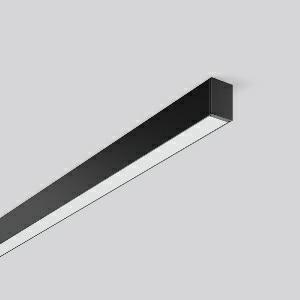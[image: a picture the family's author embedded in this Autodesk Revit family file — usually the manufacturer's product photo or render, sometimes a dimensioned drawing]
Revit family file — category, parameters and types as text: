
# Revit family: less_is_more_27_312197_003_5a47
name_source: partatom
category: Lighting Fixtures
units: mm (PartAtom-declared; Revit-internal decimal feet)

## family parameters
Cut with Voids When Loaded = No
Host = Face
Light Source = No
Part Type = Normal
Room Calculation Point = No
Round Connector Dimension = Use Diameter
Shared = No

## types (1)
- LESS IS MORE 27 (1 x LED Modul 830, 1800 lm, 3000)
    Apparent Load = 29 VA
    CIE Flux Codes = 65 89 98 100 100
    Color Rendering = 80
    Color Temperature = 3000
    Default Elevation = 1800 mm  [stored 5.90551 ft]
    Description = Series: LESS IS MORE 27
Ceiling luminaire with slim design. Housing: extruded aluminium profile, powder-coated. End cap aluminium powder-coated. Diffuser made of non-yellowing plastic (PMMA) microprismatic. Suitable for Ceiling mounting, Wall (surface). External driver with connecting cable. 
Colour: deep black, matt (RAL 9005)
Length: 1012 mm
Width: 28 mm
Height: 38 mm
Lamp: LED
Socket: without socket
Colour temperature: 3000K
Colour rendering index (CRI): 82
System power: 29 W
Rated luminous flux: 1800 lm
Luminous efficiency: 62 lm/W
Control gear: Regulated power supply
Protection class: II
Type of protection: IP 20
    Height = 38 mm
    Lamp = 1 x LED Modul 830
    Lamp Light Flux = 1800 lm
    Lamp count = 1
    Length = 1012 mm
    Lifetime = 50000 h
    Luminous efficacy = 62 lm/W
    Manufacturer = RZB
    ModVariant = No
    Model = 312197.003
    Mounting Place = Ceiling, Wall
    Mounting Type = Surface mounted
    Number of Poles = 1
    OnlyDefault = Yes
    Power Factor = 1
    Product Name = LESS IS MORE 27
    Product group = Surface mounted LED linear luminaires
    ProductGroupID = 307
    Protection Class = Protection class II
    Protection Degree = IP 20
    RLX_Detail_Level = 1
    RLX_Emergency_Light_Flux = 0 lm
    RLX_Emergency_Type = 0
    RLX_Emergency_Type_DB = No
    RlxData = <blob elided: 29977 chars, md5=b8380d6c>
    Socket = socket
    Standby Power = 0 W
    System Light Flux = 1800 lm
    System Power = 29 W
    Type Comments = Product without accessories
    Type Image = 312196.003.jpg
    URL = http://relux.com
    VarID = ---
    Voltage = 230 V
    Voltage Range = 220-240 V
    Weight = 0.00 kg
    Width = 28 mm

note: [stored X ft] marks values corroborated as IEEE doubles in the binary element streams (Revit-internal decimal feet)

## geometry (parser evidence)
native form markers: Blend x4, Sweep x12
no freeform markers — native parametric forms only
